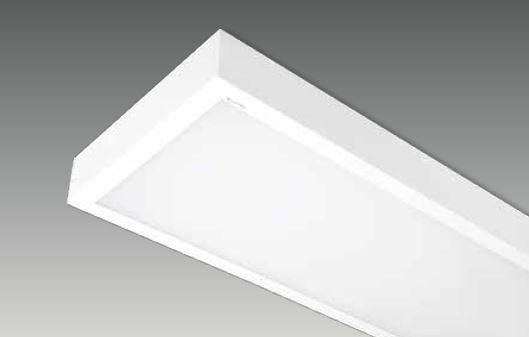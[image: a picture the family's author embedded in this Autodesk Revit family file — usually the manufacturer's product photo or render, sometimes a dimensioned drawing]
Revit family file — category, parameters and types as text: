
# Revit family: SD 3012 OPL
name_source: partatom
category: Lighting Fixtures
revit_build: Autodesk Revit 2017 (Build: 20160225_1515(x64)
units: mm (PartAtom-declared; Revit-internal decimal feet)

## family parameters
Cut with Voids When Loaded = No
Host = Face
Light Source = Yes
Part Type = Normal
Room Calculation Point = No
Round Connector Dimension = Use Diameter
Shared = No

## types (2) — shared parameters
Color Filter = 16777215
Default Elevation = 1219 mm
Dimming Lamp Color Temperature Shift = <None>
Emit Shape Visible in Rendering = Yes
Emit from Rectangle Length = 1170 mm  [stored 3.83858 ft]
Emit from Rectangle Width = 305 mm  [stored 1.00066 ft]
Light Source Symbol Size = 610 mm
Manufacturer = ARLIGHT
Type Image = SD 3012 OPL.JPG
Wattage Comments = 36

## type names (no varying parameters)
- SDOPL.3012.36.30
- SDOPL.3012.36.40

note: [stored X ft] marks values corroborated as IEEE doubles in the binary element streams (Revit-internal decimal feet)

## geometry (parser evidence)
native form markers: Sweep x3
no freeform markers — native parametric forms only
